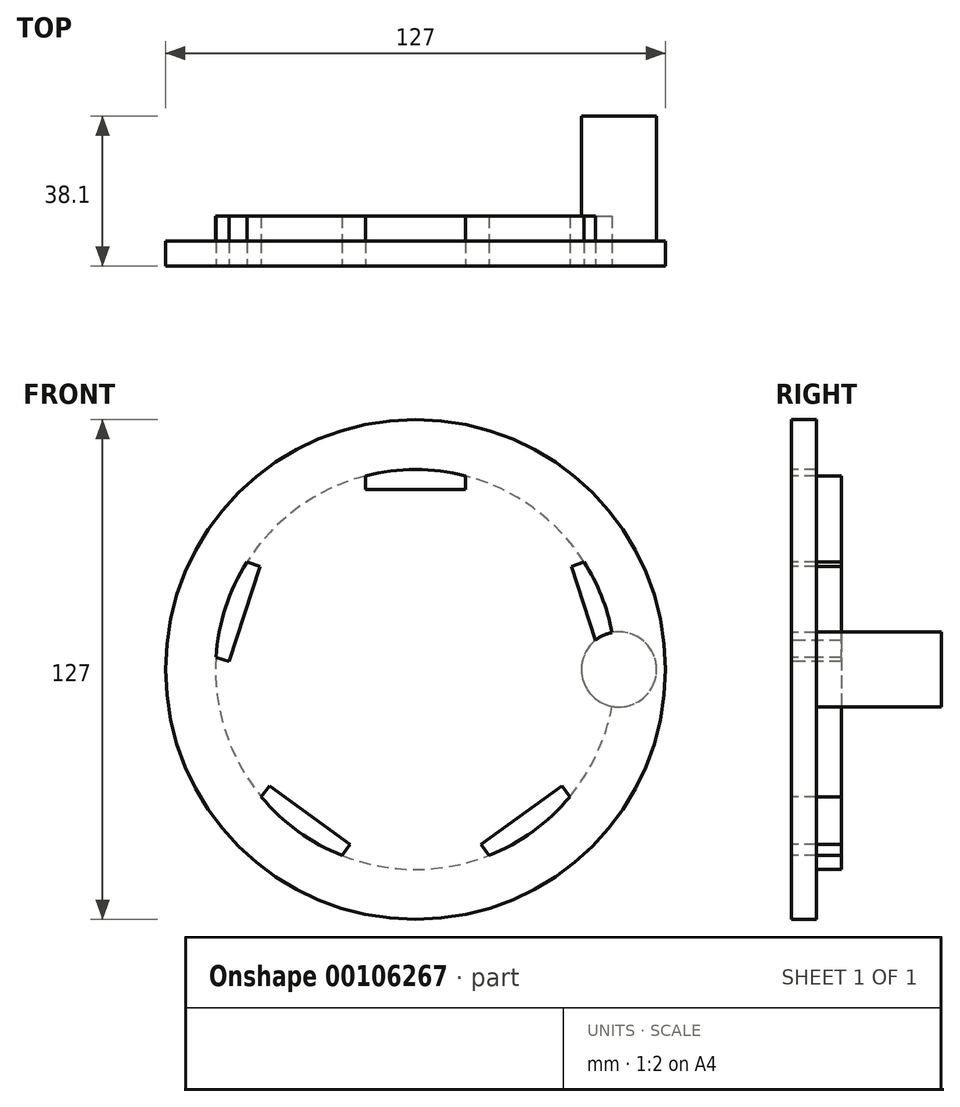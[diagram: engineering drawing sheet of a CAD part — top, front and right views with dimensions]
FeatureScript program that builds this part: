
annotation { "Feature Type Name" : "Feature", "Feature Type Description" : "" }
export const myFeature = defineFeature(function(context is Context, id is Id, definition is map)
    precondition{}
    {
        {
            var Q0;
            Q0=qCreatedBy(makeId("Front.planeOp"),FACE);
            var sketch = newSketch(context, id + "F0", { "sketchPlane" : qUnion([Q0])});
            skCircle(sketch, "E0", {"center": v(0, 0) * mm, "radius": 63.5 * mm});
            skCircle(sketch, "E1", {"center": v(0, 0) * mm, "radius": 50.8 * mm});
            skPoint(sketch, "E2.0.midPoint", {"position": v(0, 31.75) * mm});
            skLineSegment(sketch, "E3", {"start": v(-12.7, 45.72) * mm, "end": v(-12.7, 49.19) * mm});
            skLineSegment(sketch, "E4.MirrorCS", {"start": v(12.7, 45.72) * mm, "end": v(12.7, 49.19) * mm});
            skLineSegment(sketch, "E5", {"start": v(-12.7, 49.19) * mm, "end": v(-12.7, 52.07) * mm});
            skLineSegment(sketch, "E6.MirrorCS", {"start": v(12.7, 49.19) * mm, "end": v(12.7, 52.07) * mm});
            skLineSegment(sketch, "E7", {"start": v(12.7, 52.07) * mm, "end": v(-12.7, 52.07) * mm});
            skLineSegment(sketch, "E8", {"start": v(39.56, 26.2) * mm, "end": v(42.85, 27.28) * mm});
            skLineSegment(sketch, "E9", {"start": v(42.85, 27.28) * mm, "end": v(45.6, 28.17) * mm});
            skLineSegment(sketch, "E10.MirrorCS", {"start": v(50.7, 3.12) * mm, "end": v(53.45, 4.01) * mm});
            skLineSegment(sketch, "E11", {"start": v(45.6, 28.17) * mm, "end": v(53.45, 4.01) * mm});
            skLineSegment(sketch, "E12.MirrorCS", {"start": v(-39.56, 26.2) * mm, "end": v(-42.85, 27.28) * mm});
            skLineSegment(sketch, "E13.MirrorCS", {"start": v(-45.6, 28.17) * mm, "end": v(-53.45, 4.01) * mm});
            skLineSegment(sketch, "E14.MirrorCS", {"start": v(-47.4, 2.05) * mm, "end": v(-53.45, 4.01) * mm});
            skLineSegment(sketch, "E15.MirrorCS", {"start": v(-50.7, 3.12) * mm, "end": v(-53.45, 4.01) * mm});
            skLineSegment(sketch, "E16.MirrorCS", {"start": v(-42.85, 27.28) * mm, "end": v(-45.6, 28.17) * mm});
            skLineSegment(sketch, "E17", {"start": v(37.15, -29.52) * mm, "end": v(40.88, -34.66) * mm});
            skLineSegment(sketch, "E18.MirrorCS", {"start": v(16.6, -44.45) * mm, "end": v(20.33, -49.6) * mm});
            skLineSegment(sketch, "E19", {"start": v(40.88, -34.66) * mm, "end": v(20.33, -49.6) * mm});
            skLineSegment(sketch, "E20.MirrorCS", {"start": v(-37.15, -29.52) * mm, "end": v(-40.88, -34.66) * mm});
            skLineSegment(sketch, "E21.MirrorCS", {"start": v(-40.88, -34.66) * mm, "end": v(-20.33, -49.6) * mm});
            skLineSegment(sketch, "E22.MirrorCS", {"start": v(-16.6, -44.45) * mm, "end": v(-20.33, -49.6) * mm});
            skLineSegment(sketch, "E23", {"start": v(39.56, 26.2) * mm, "end": v(47.4, 2.05) * mm});
            skLineSegment(sketch, "E24", {"start": v(37.15, -29.52) * mm, "end": v(16.6, -44.45) * mm});
            skLineSegment(sketch, "E25", {"start": v(-16.6, -44.45) * mm, "end": v(-37.15, -29.52) * mm});
            skLineSegment(sketch, "E26", {"start": v(-47.4, 2.05) * mm, "end": v(-39.56, 26.2) * mm});
            skLineSegment(sketch, "E27", {"start": v(-12.7, 45.72) * mm, "end": v(12.7, 45.72) * mm});
            skLineSegment(sketch, "E28", {"start": v(50.7, 3.12) * mm, "end": v(47.4, 2.05) * mm});
            skSolve(sketch);
        }
        {
            var Q0;
            Q0=makeQuery(id+"F0.imprint","IMPRINT",FACE,{"disambiguationData":[TD([[makeQuery(id+"F0.imprint","IMPRINT",EDGE,{"derivedFrom":sQuery(id+"F0.wireOp",EDGE,"E0")}),1.0]])]});
            var Q1;
            {var subQ5=sQuery(id+"F0.wireOp",EDGE,"E21.MirrorCS");Q1=makeQuery(id+"F0.imprint","IMPRINT",FACE,{"disambiguationData":[TD([[makeQuery(id+"F0.imprint","IMPRINT",EDGE,{"derivedFrom":subQ5}),1.0]])]});}
            var Q2;
            Q2=makeQuery(id+"F0.imprint","IMPRINT",FACE,{"disambiguationData":[TD([[makeQuery(id+"F0.imprint","IMPRINT",EDGE,{"derivedFrom":sQuery(id+"F0.wireOp",EDGE,"E13.MirrorCS")}),1.0]])]});
            var Q3;
            {var subQ5=sQuery(id+"F0.wireOp",EDGE,"E19");Q3=makeQuery(id+"F0.imprint","IMPRINT",FACE,{"disambiguationData":[TD([[makeQuery(id+"F0.imprint","IMPRINT",EDGE,{"derivedFrom":subQ5}),-1.0]])]});}
            var Q4;
            {var subQ0=sQuery(id+"F0.wireOp",EDGE,"E9");Q4=makeQuery(id+"F0.imprint","IMPRINT",FACE,{"disambiguationData":[TD([[makeQuery(id+"F0.imprint","IMPRINT",EDGE,{"derivedFrom":subQ0}),-1.0]])]});}
            var Q5;
            {var subQ0=sQuery(id+"F0.wireOp",EDGE,"E5");Q5=makeQuery(id+"F0.imprint","IMPRINT",FACE,{"disambiguationData":[TD([[makeQuery(id+"F0.imprint","IMPRINT",EDGE,{"derivedFrom":subQ0}),-1.0]])]});}
            extrude(context, id + "F1", {"entities" : qUnion([Q0, Q1, Q2, Q3, Q4, Q5]), "oppositeDirection" : true, "depth" : 6.35 * mm});
        }
        {
            var Q0;
            {var subQ2=sQuery(id+"F0.wireOp",EDGE,"E3");Q0=makeQuery(id+"F0.imprint","IMPRINT",FACE,{"disambiguationData":[TD([[makeQuery(id+"F0.imprint","IMPRINT",EDGE,{"derivedFrom":subQ2}),1.0]])]});}
            extrude(context, id + "F2", {"entities" : qUnion([Q0]), "operationType" : NewBodyOperationType.ADD, "oppositeDirection" : true, "depth" : 12.7 * mm});
        }
        {
            var Q0;
            Q0=qCreatedBy(makeId("Front.planeOp"),FACE);
            var sketch = newSketch(context, id + "F3", { "sketchPlane" : qUnion([Q0])});
            skCircle(sketch, "E29", {"center": v(51.7, 0) * mm, "radius": 9.53 * mm});
            skSolve(sketch);
        }
        {
            var Q0;
            Q0 = qSketchRegion(id + "F3", true);
            extrude(context, id + "F4", {"entities" : qUnion([Q0]), "operationType" : NewBodyOperationType.ADD, "oppositeDirection" : true, "depth" : 38.1 * mm});
        }
        {
            var Q0;
            Q0=qCreatedBy(makeId("Top.planeOp"),FACE);
            var sketch = newSketch(context, id + "F5", { "sketchPlane" : qUnion([Q0])});
            skLineSegment(sketch, "E30", {"start": v(0, -38.95) * mm, "end": v(0, 50.5) * mm, "construction": true});
            skSolve(sketch);
        }
    });
